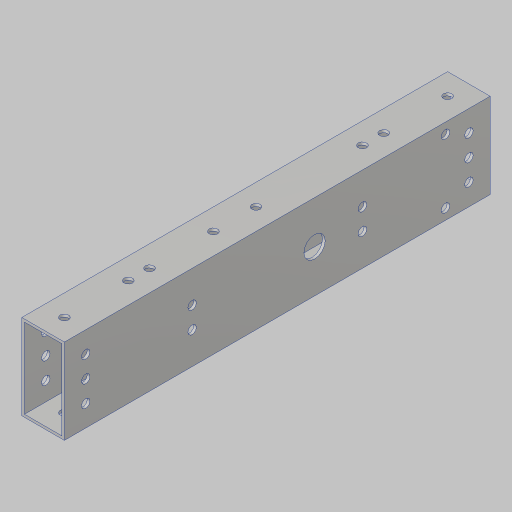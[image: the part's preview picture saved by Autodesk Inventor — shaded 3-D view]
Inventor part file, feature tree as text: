
AUTODESK INVENTOR PART (.ipt)
format: ipt  version: 2023.5 (Build 275446000, 446)  size: 215,040 bytes
history: native  units: in
note: dims shown in document units (in); Inventor stores cm internally (conversion verified against a paired STEP export)
features: sketch x8, hole x7, projected_geometry x3, extrude x2, mirror x1
ambient origin geometry x8: Origin, YZ Plane, XZ Plane, XY Plane, X Axis, Y Axis, Z Axis, Center Point
bodies: Solid1 (feature_tree)
feature tree (21):
  extrude  "Extrusion1"  Depth=0.5in
  hole  "Block Mount Holes"  [1 undecoded]
  hole  "Hole3"  [1 undecoded]
  hole  "Hole5"  [1 undecoded]
  hole  "Hole6"  [1 undecoded]
  sketch  "Sketch10"  dims[d29=0.201in d30=0.75in d31=0.385in d32=0.25in d33=0.5635in d34=1.0in d35=0.8108in d61=0.5in]
  hole  "Hole8"  [1 undecoded]
  hole  "Hole9"  [1 undecoded]
  mirror  "Mirror1"
  extrude  "Extrusion5"  Depth=0.0625in
  hole  "Hole10"  [1 undecoded]
  sketch  "Sketch2"  dims[d4=0.0in d5=0.5in]
  sketch  "Sketch4"  dims[d6=0.5in d7=0.5in]
  sketch  "Sketch8"  dims[d8=0.5in]
  sketch  "Sketch9"  dims[d9=0.201in d10=0.75in d11=0.385in d12=0.25in d13=0.5635in d14=1.0in d15=0.8108in]
  sketch  "Sketch11"  dims[d65=5.0in d66=0.5in]
  sketch  "Sketch13"  dims[d67=1.0in d68=1.0in]
  sketch  "Sketch14"  dims[d69=0.201in d70=0.75in d71=0.385in d72=0.25in d73=0.5635in d74=1.0in d75=0.8108in d79=0.5in d80=0.5in d81=0.201in d82=0.75in d83=0.385in d84=0.25in d85=0.5635in d86=1.0in d87=0.8108in d88=2.75in d89=1.175in d97=4.125in d98=0.201in d99=0.75in d100=0.375in d101=0.25in d102=0.5635in d103=1.0in d104=0.8108in d105=3.0in d106=0.5in d107=0.201in d108=0.75in d109=0.375in d110=0.25in d111=0.5635in d112=1.0in d113=0.8108in d117=0.5in d118=1.0in d119=0.0in d120=1.5in d121=1.0497in d122=0.201in d123=0.38in d124=0.385in d125=0.25in d126=0.5635in d127=1.0in d128=0.8108in d44=1.0in d45=1.0in d46=1.0in d47=0.15in d48=0.25in d49=0.375in d50=0.5635in d51=0.75in d52=0.8108in d53=0.0625in d54=0.75in d55=0.375in]
  projected_geometry  "Project Cut Edges1"
  projected_geometry  "Project Cut Edges4"
  projected_geometry  "Project Cut Edges6"
note: 7 required parameter values undecoded (feature->parameter linkage not recoverable at this tier; creation-order binding heuristic only, values carry confidence <= 0.55)
